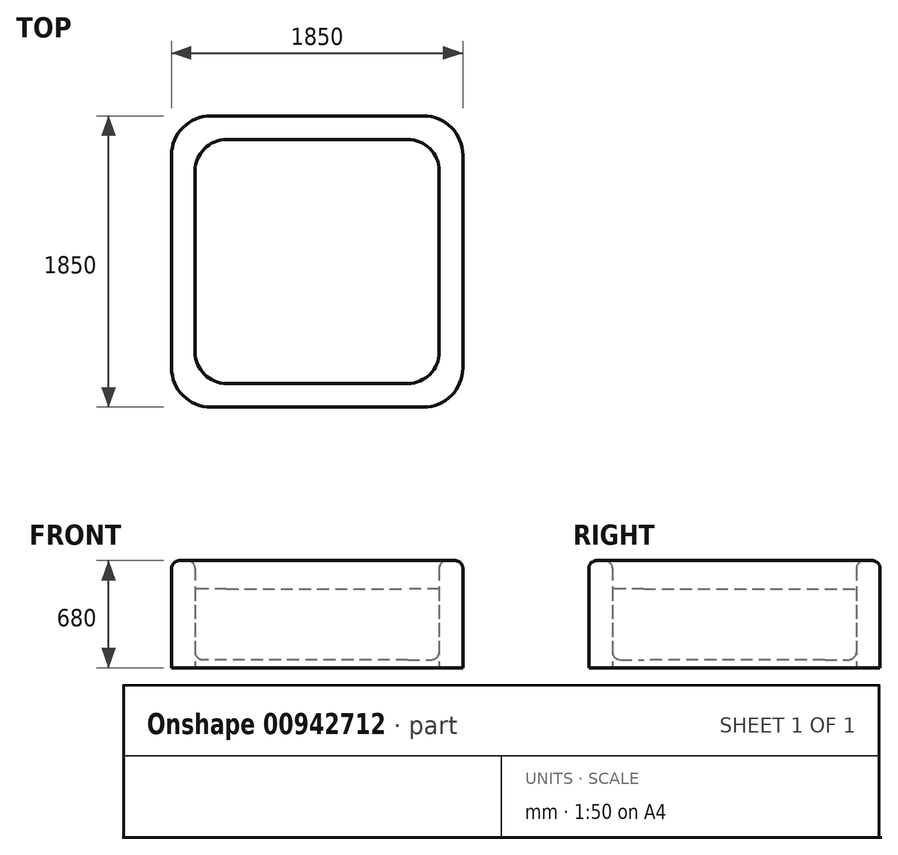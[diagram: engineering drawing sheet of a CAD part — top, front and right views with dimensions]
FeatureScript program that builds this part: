
annotation { "Feature Type Name" : "Feature", "Feature Type Description" : "" }
export const myFeature = defineFeature(function(context is Context, id is Id, definition is map)
    precondition{}
    {
        {
            var Q0;
            Q0=qCreatedBy(makeId("Top.planeOp"),FACE);
            var sketch = newSketch(context, id + "F0", { "sketchPlane" : qUnion([Q0])});
            skLineSegment(sketch, "E0.bottom", {"start": v(-675, -925) * mm, "end": v(675, -925) * mm});
            skLineSegment(sketch, "E0.top", {"start": v(-675, 925) * mm, "end": v(675, 925) * mm});
            skLineSegment(sketch, "E0.left", {"start": v(-925, -675) * mm, "end": v(-925, 675) * mm});
            skLineSegment(sketch, "E0.right", {"start": v(925, -675) * mm, "end": v(925, 675) * mm});
            skLineSegment(sketch, "E1", {"start": v(-925, 0) * mm, "end": v(0, 0) * mm, "construction": true});
            skLineSegment(sketch, "E2", {"start": v(0, 0) * mm, "end": v(925, 0) * mm, "construction": true});
            skLineSegment(sketch, "E3", {"start": v(0, -925) * mm, "end": v(0, 0) * mm, "construction": true});
            skLineSegment(sketch, "E4", {"start": v(0, 0) * mm, "end": v(0, 925) * mm, "construction": true});
            skPoint(sketch, "E5.visualSharp", {"position": v(-925, 925) * mm});
            skArc(sketch, "E5.filletArc", {"start": v(-675, 925) * mm, "mid": v(-851.78, 851.78) * mm, "end": v(-925, 675) * mm});
            skPoint(sketch, "E6.visualSharp", {"position": v(925, 925) * mm});
            skArc(sketch, "E6.filletArc", {"start": v(925, 675) * mm, "mid": v(851.78, 851.78) * mm, "end": v(675, 925) * mm});
            skPoint(sketch, "E7.visualSharp", {"position": v(925, -925) * mm});
            skArc(sketch, "E7.filletArc", {"start": v(675, -925) * mm, "mid": v(851.78, -851.78) * mm, "end": v(925, -675) * mm});
            skPoint(sketch, "E8.visualSharp", {"position": v(-925, -925) * mm});
            skArc(sketch, "E8.filletArc", {"start": v(-925, -675) * mm, "mid": v(-851.78, -851.78) * mm, "end": v(-675, -925) * mm});
            skLineSegment(sketch, "E9.bottom", {"start": v(-575, -775) * mm, "end": v(575, -775) * mm});
            skLineSegment(sketch, "E9.top", {"start": v(-575, 775) * mm, "end": v(575, 775) * mm});
            skLineSegment(sketch, "E9.left", {"start": v(-775, -575) * mm, "end": v(-775, 575) * mm});
            skLineSegment(sketch, "E9.right", {"start": v(775, -575) * mm, "end": v(775, 575) * mm});
            skPoint(sketch, "E10.visualSharp", {"position": v(-775, 775) * mm});
            skArc(sketch, "E10.filletArc", {"start": v(-575, 775) * mm, "mid": v(-716.42, 716.42) * mm, "end": v(-775, 575) * mm});
            skPoint(sketch, "E11.visualSharp", {"position": v(775, 775) * mm});
            skArc(sketch, "E11.filletArc", {"start": v(775, 575) * mm, "mid": v(716.42, 716.42) * mm, "end": v(575, 775) * mm});
            skPoint(sketch, "E12.visualSharp", {"position": v(775, -775) * mm});
            skArc(sketch, "E12.filletArc", {"start": v(575, -775) * mm, "mid": v(716.42, -716.42) * mm, "end": v(775, -575) * mm});
            skPoint(sketch, "E13.visualSharp", {"position": v(-775, -775) * mm});
            skArc(sketch, "E13.filletArc", {"start": v(-775, -575) * mm, "mid": v(-716.42, -716.42) * mm, "end": v(-575, -775) * mm});
            skSolve(sketch);
        }
        {
            var Q0;
            Q0=makeQuery(id+"F0.imprint","IMPRINT",FACE,{"disambiguationData":[TD([[makeQuery(id+"F0.imprint","IMPRINT",EDGE,{"derivedFrom":sQuery(id+"F0.wireOp",EDGE,"E9.bottom")}),1.0]])]});
            var Q1;
            Q1=makeQuery(id+"F0.imprint","IMPRINT",FACE,{"disambiguationData":[TD([[makeQuery(id+"F0.imprint","IMPRINT",EDGE,{"derivedFrom":sQuery(id+"F0.wireOp",EDGE,"E0.bottom")}),1.0]])]});
            extrude(context, id + "F1", {"entities" : qUnion([Q0, Q1]), "depth" : 50 * mm, "offsetDistance" : 25 * mm});
        }
        {
            var Q0;
            Q0=makeQuery(id+"F0.imprint","IMPRINT",FACE,{"disambiguationData":[TD([[makeQuery(id+"F0.imprint","IMPRINT",EDGE,{"derivedFrom":sQuery(id+"F0.wireOp",EDGE,"E0.bottom")}),1.0]])]});
            extrude(context, id + "F2", {"entities" : qUnion([Q0]), "operationType" : NewBodyOperationType.ADD, "depth" : 680 * mm, "offsetDistance" : 25 * mm});
        }
        {
            var Q0;
            Q0=makeQuery(id+"F2.opExtrude","CAP_FACE",FACE,{"disambiguationData":[OSD([sQuery(id+"F0.wireOp",EDGE,"E0.bottom"),sQuery(id+"F0.wireOp",EDGE,"E0.top"),sQuery(id+"F0.wireOp",EDGE,"E0.left"),sQuery(id+"F0.wireOp",EDGE,"E0.right"),sQuery(id+"F0.wireOp",EDGE,"E5.filletArc"),sQuery(id+"F0.wireOp",EDGE,"E6.filletArc"),sQuery(id+"F0.wireOp",EDGE,"E7.filletArc"),sQuery(id+"F0.wireOp",EDGE,"E8.filletArc"),sQuery(id+"F0.wireOp",EDGE,"E9.bottom"),sQuery(id+"F0.wireOp",EDGE,"E9.top"),sQuery(id+"F0.wireOp",EDGE,"E9.left"),sQuery(id+"F0.wireOp",EDGE,"E9.right"),sQuery(id+"F0.wireOp",EDGE,"E10.filletArc"),sQuery(id+"F0.wireOp",EDGE,"E11.filletArc"),sQuery(id+"F0.wireOp",EDGE,"E12.filletArc"),sQuery(id+"F0.wireOp",EDGE,"E13.filletArc")])],"isStart":false});
            var Q1;
            Q1=makeQuery(id+"F1.opExtrude","CAP_FACE",FACE,{"disambiguationData":[OSD([sQuery(id+"F0.wireOp",EDGE,"E0.bottom"),sQuery(id+"F0.wireOp",EDGE,"E0.top"),sQuery(id+"F0.wireOp",EDGE,"E0.left"),sQuery(id+"F0.wireOp",EDGE,"E0.right"),sQuery(id+"F0.wireOp",EDGE,"E5.filletArc"),sQuery(id+"F0.wireOp",EDGE,"E6.filletArc"),sQuery(id+"F0.wireOp",EDGE,"E7.filletArc"),sQuery(id+"F0.wireOp",EDGE,"E8.filletArc")])],"isStart":false});
            fillet(context, id + "F3", {"entities" : qUnion([Q0, Q1]), "radius" : 50 * mm, "tangentPropagation" : true, "allowEdgeOverflow" : false});
        }
        {
            var Q0;
            Q0=makeQuery(id+"F0.imprint","IMPRINT",FACE,{"disambiguationData":[TD([[makeQuery(id+"F0.imprint","IMPRINT",EDGE,{"derivedFrom":sQuery(id+"F0.wireOp",EDGE,"E9.bottom")}),1.0]])]});
            extrude(context, id + "F4", {"entities" : qUnion([Q0]), "depth" : 500 * mm, "offsetDistance" : 25 * mm});
        }
    });
